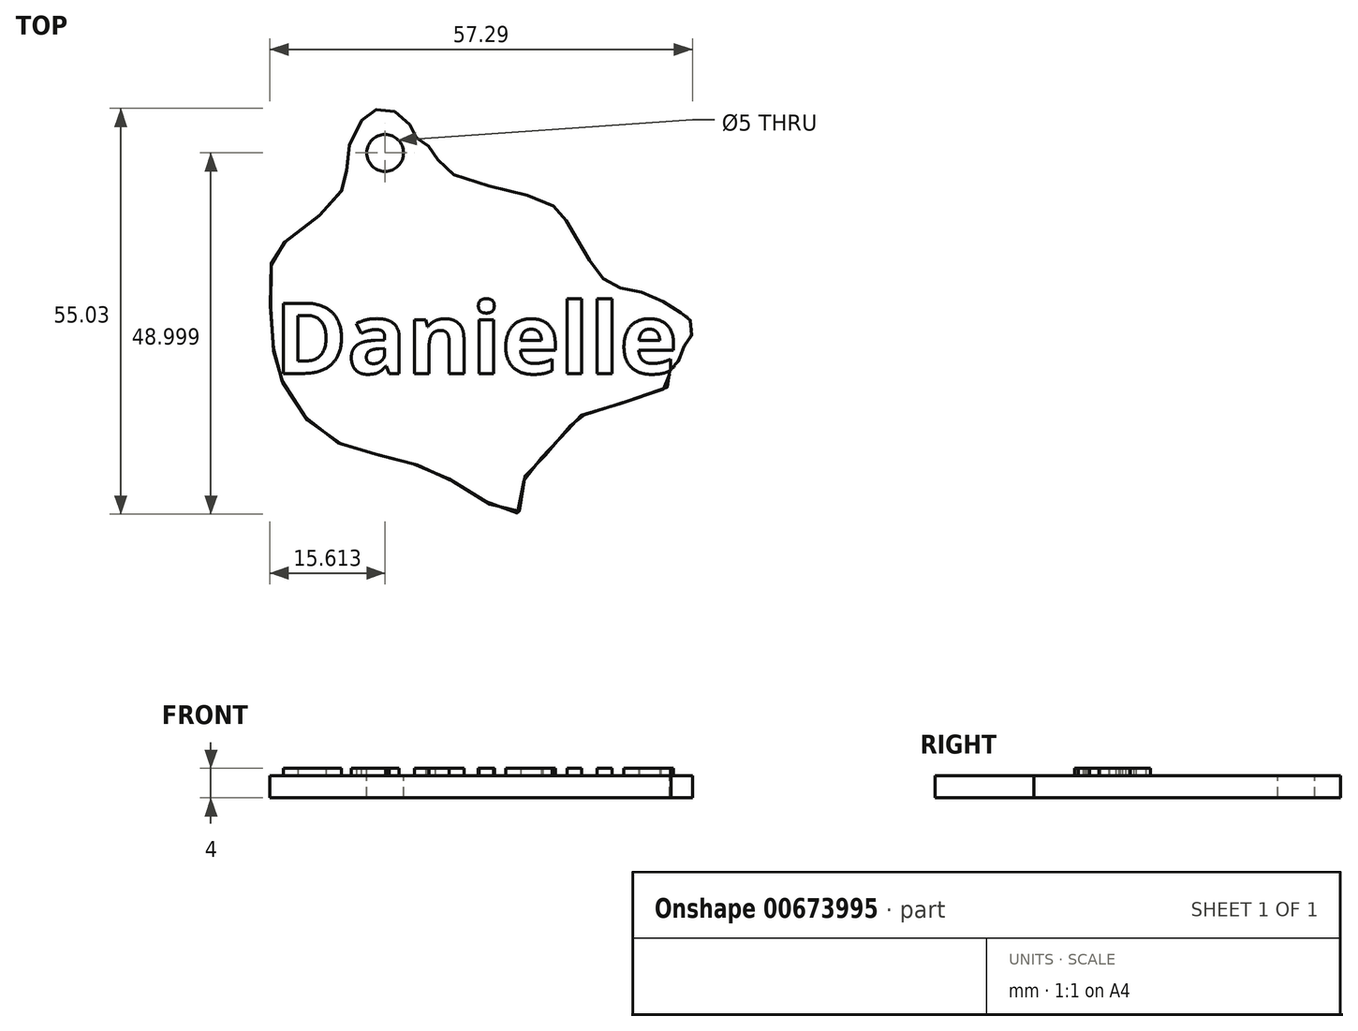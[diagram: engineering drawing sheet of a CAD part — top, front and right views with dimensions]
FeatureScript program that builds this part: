
annotation { "Feature Type Name" : "Feature", "Feature Type Description" : "" }
export const myFeature = defineFeature(function(context is Context, id is Id, definition is map)
    precondition{}
    {
        {
            var Q0;
            Q0=qCreatedBy(makeId("Top.planeOp"),FACE);
            var sketch = newSketch(context, id + "F0", { "sketchPlane" : qUnion([Q0])});
            skFitSpline(sketch, "E0", {"points": [v(-54.35, 60.67) * mm, v(-56, 57.37) * mm, v(-56.36, 54.07) * mm, v(-56.73, 52.06) * mm, v(-58.38, 49.3) * mm, v(-65.16, 43.8) * mm, v(-66.63, 41.06) * mm, v(-66.45, 31.34) * mm, v(-65.35, 25.85) * mm, v(-60.03, 18.51) * mm, v(-53.07, 15.58) * mm, v(-45.73, 13.56) * mm, v(-38.58, 9.71) * mm, v(-33.09, 7.52) * mm, v(-31.99, 13.2) * mm, v(-28.5, 15.95) * mm, v(-25.02, 20.71) * mm, v(-24.47, 20.71) * mm, v(-14.76, 23.83) * mm, v(-12.37, 25.11) * mm, v(-12.56, 26.76) * mm, v(-11.64, 27.5) * mm, v(-10.72, 29.88) * mm, v(-9.62, 31.34) * mm, v(-9.8, 33.73) * mm, v(-11.09, 34.64) * mm, v(-15.67, 37.2) * mm, v(-20.25, 38.3) * mm, v(-23.55, 41.98) * mm, v(-26.49, 46.92) * mm, v(-29.79, 49.86) * mm, v(-42.8, 53.89) * mm, v(-44.82, 56.82) * mm, v(-46.83, 58.29) * mm, v(-47.93, 60.3) * mm, v(-51.42, 62.32) * mm, v(-54.35, 60.67) * mm]});
            skSolve(sketch);
        }
        {
            var Q0;
            Q0 = qSketchRegion(id + "F0", true);
            var Q1;
            Q1=makeQuery(id+"F0.imprint","IMPRINT",FACE,{"disambiguationData":[TD([[makeQuery(id+"F0.imprint","IMPRINT",EDGE,{"derivedFrom":sQuery(id+"F0.wireOp",EDGE,"E0")}),1.0]])]});
            extrude(context, id + "F1", {"entities" : qUnion([Q0, Q1]), "depth" : 3 * mm, "offsetDistance" : 25 * mm});
        }
        {
            var Q0;
            Q0=makeQuery(id+"F1.opExtrude","CAP_FACE",FACE,{"disambiguationData":[OSD([sQuery(id+"F0.wireOp",EDGE,"E0")])],"isStart":false});
            var sketch = newSketch(context, id + "F2", { "sketchPlane" : qUnion([Q0])});
            skCircle(sketch, "E1", {"center": v(-51.15, 56.29) * mm, "radius": 2.5 * mm});
            skSolve(sketch);
        }
        {
            var Q0;
            Q0=sQuery(id+"F2.wireOp",VERTEX,"E1.center");
            var Q1;
            Q1=makeQuery(id+"F1.opExtrude","SWEPT_BODY",BODY,{"disambiguationData":[OSD([sQuery(id+"F0.wireOp",EDGE,"E0")])]});
            hole(context, id + "F3", {"style" : HoleStyle.SIMPLE, "endStyle" : HoleEndStyle.THROUGH, "holeDiameter" : 5 * mm, "majorDiameter" : 5 * mm, "isTappedThrough" : true, "tappedDepth" : 12 * mm, "tapClearance" : 3, "locations" : qUnion([Q0]), "scope" : qUnion([Q1])});
        }
        {
            var Q0;
            Q0=makeQuery(id+"F1.opExtrude","CAP_FACE",FACE,{"disambiguationData":[OSD([sQuery(id+"F0.wireOp",EDGE,"E0")])],"isStart":false});
            var sketch = newSketch(context, id + "F4", { "sketchPlane" : qUnion([Q0])});
            skText(sketch, "E2", { "text": "Danielle ", "fontName": "OpenSans-Bold.ttf"});
            const initialGuessF4  = {"E2": [-0.06617, 0.02637, 1, 0, 0.00961]};
            skSetInitialGuess(sketch, initialGuessF4);
            skSolve(sketch);
        }
        {
            var Q0;
            Q0 = qSketchRegion(id + "F4", true);
            extrude(context, id + "F5", {"entities" : qUnion([Q0]), "operationType" : NewBodyOperationType.ADD, "depth" : 1 * mm, "offsetDistance" : 25 * mm});
        }
    });
